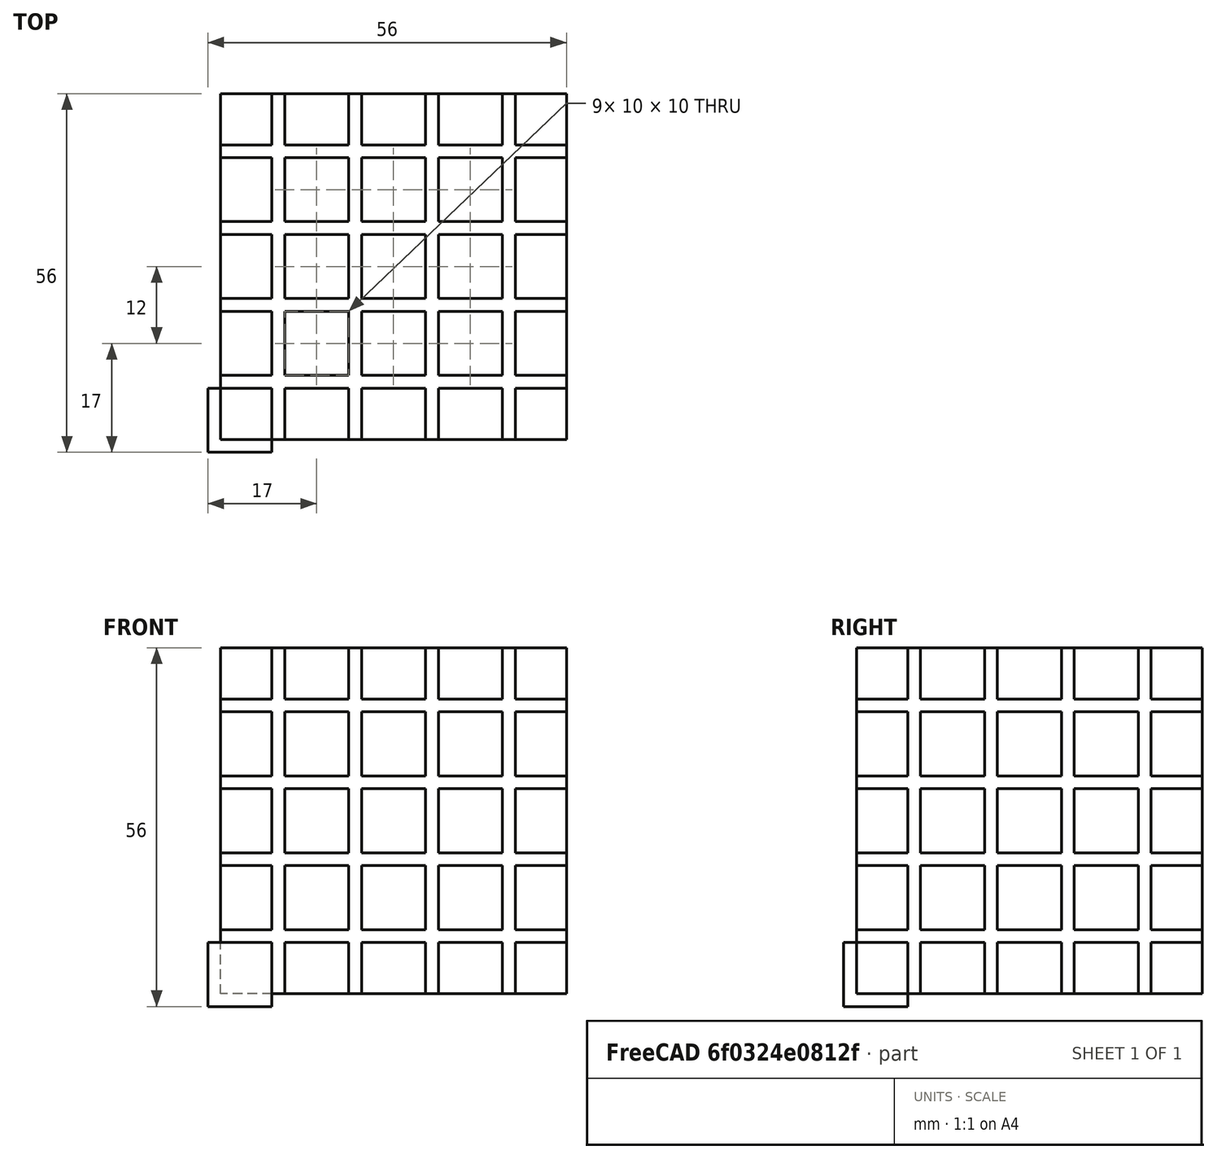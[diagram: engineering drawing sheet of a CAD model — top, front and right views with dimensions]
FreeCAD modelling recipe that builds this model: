
FCSTD DOCUMENT  (FreeCAD 1.0R39319 (Git))
Label: ojt1_t10p01
License: All rights reserved
LicenseURL: https://en.wikipedia.org/wiki/All_rights_reserved
objects: Part::Box×2, Part::FeaturePython×1, Part::Cut×1
note: 3 computed .brp shape members not serialized (recipe doc carries the construction recipe); baked Part::Feature solids carry a one-line shape summary decoded from their .brp

FEATURE [Part::Box] Box005  label="Cub005"
  AttacherType = Attacher::AttachEngine3D
  Height = 10
  Length = 10
  Width = 10
FEATURE [Part::FeaturePython] Array003  # Draft array (typed FeaturePython)
  AlwaysSyncPlacement = false
  Angle = 360
  ArrayType = 0
  Axis = (0,0,1)
  Base = -> Box005
  Center = (0,0,0)
  Count = 125
  ExpandArray = false
  Fuse = false
  IntervalAxis = (0,0,0)
  IntervalX = (12,0,0)
  IntervalY = (0,12,0)
  IntervalZ = (0,0,12)
  NumberCircles = 3
  NumberPolar = 5
  NumberX = 5
  NumberY = 5
  NumberZ = 5
  PlacementList = 125 placements: [(0,0,0),(0,0,12),(0,0,24),(0,0,36),(0,0,48),(0,12,0),(0,12,12),(0,12,24),(0,12,36),(0,12,48),(0,24,0),(0,24,12),(0,24,24),(0,24,36),(0,24,48),(0,36,0),(0,36,12),(0,36,24),(0,36,36),(0,36,48),(0,48,0),(0,48,12),(0,48,24),(0,48,36),(0,48,48),(12,0,0),(12,0,12),(12,0,24),(12,0,36),(12,0,48),(12,12,0),(12,12,12),(12,12,24),(12,12,36),(12,12,48),(12,24,0),(12,24,12),(12,24,24),(12,24,36),(12,24,48),+85 more]
  RadialDistance = 50
  Symmetry = 1
  TangentialDistance = 25
FEATURE [Part::Box] Box006  label="Cub006"
  AttacherType = Attacher::AttachEngine3D
  Height = 54
  Length = 54
  Placement = pos=(2,2,2) rot=(0,0,1;0rad)
  Width = 54
FEATURE [Part::Cut] Cut002
  Base = -> Box006
  Refine = true
  Tool = -> Array003
